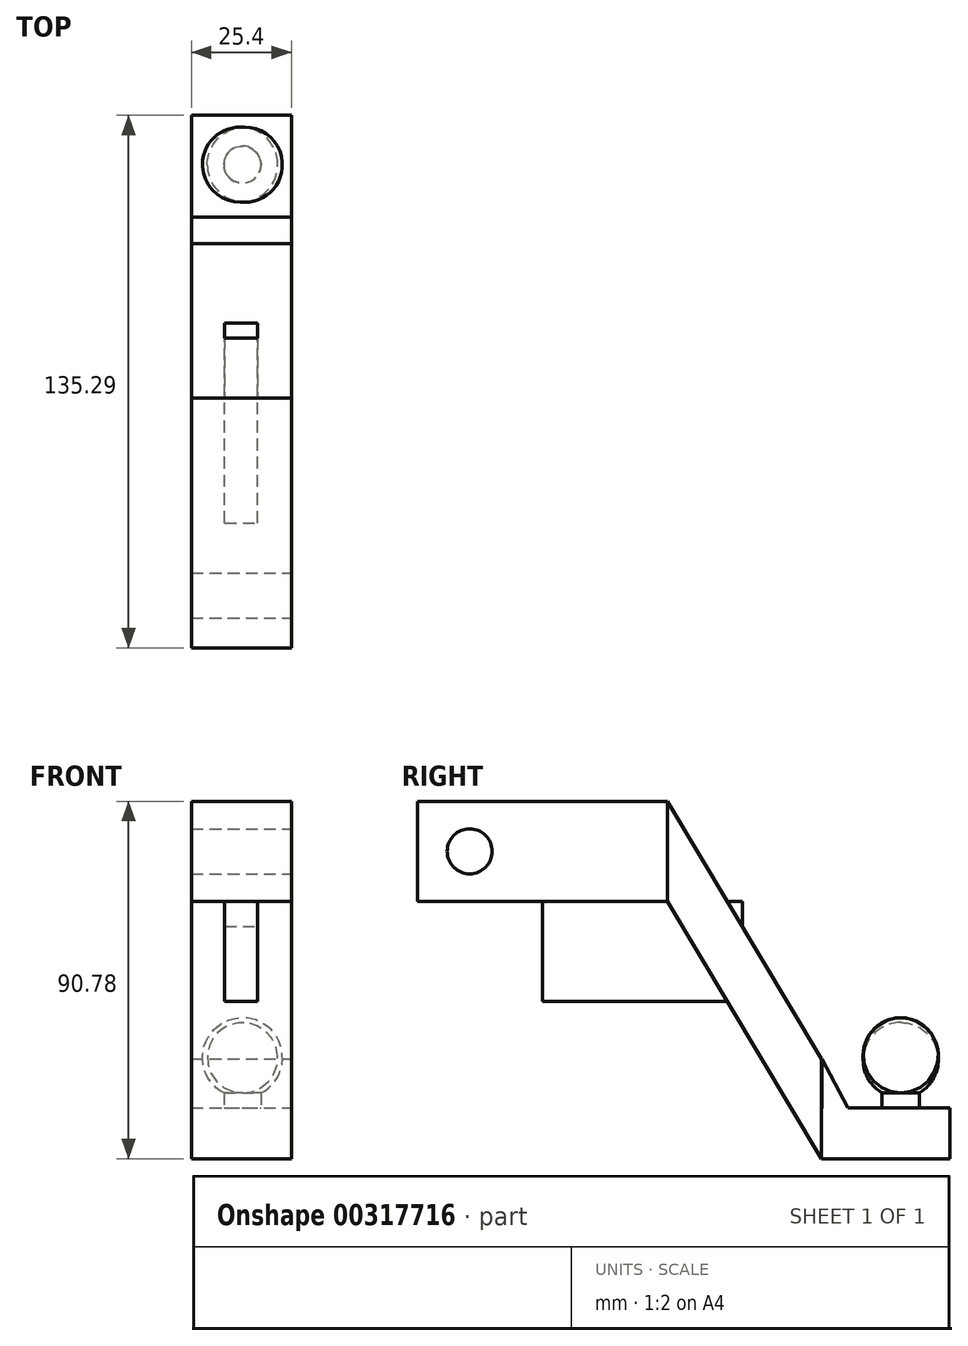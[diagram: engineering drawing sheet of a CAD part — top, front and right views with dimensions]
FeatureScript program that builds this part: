
annotation { "Feature Type Name" : "Feature", "Feature Type Description" : "" }
export const myFeature = defineFeature(function(context is Context, id is Id, definition is map)
    precondition{}
    {
        {
            var Q0;
            Q0=qCreatedBy(makeId("Front.planeOp"),FACE);
            var sketch = newSketch(context, id + "F0", { "sketchPlane" : qUnion([Q0])});
            skLineSegment(sketch, "E0", {"start": v(0, 0) * mm, "end": v(-25.4, 0) * mm});
            skLineSegment(sketch, "E1", {"start": v(-25.4, 0) * mm, "end": v(-25.4, -25.4) * mm});
            skLineSegment(sketch, "E2", {"start": v(-25.4, -25.4) * mm, "end": v(0, -25.4) * mm});
            skLineSegment(sketch, "E3", {"start": v(0, 0) * mm, "end": v(0, -25.4) * mm});
            skSolve(sketch);
        }
        {
            var Q0;
            Q0 = qSketchRegion(id + "F0", true);
            extrude(context, id + "F1", {"entities" : qUnion([Q0]), "endBound" : BoundingType.SYMMETRIC, "depth" : 63.5 * mm});
        }
        {
            var Q0;
            Q0=makeQuery(id+"F1.opExtrude","SWEPT_FACE",FACE,{"disambiguationData":[OSD([sQuery(id+"F0.wireOp",EDGE,"E3")])]});
            var sketch = newSketch(context, id + "F2", { "sketchPlane" : qUnion([Q0])});
            skCircle(sketch, "E4", {"center": v(-18.48, -12.7) * mm, "radius": 4.5 * mm});
            skSolve(sketch);
        }
        {
            var Q0;
            Q0=sQuery(id+"F2.wireOp",VERTEX,"E4.center");
            var Q1;
            Q1=makeQuery(id+"F1.opExtrude","SWEPT_BODY",BODY,{"disambiguationData":[OSD([sQuery(id+"F0.wireOp",EDGE,"E0"),sQuery(id+"F0.wireOp",EDGE,"E1"),sQuery(id+"F0.wireOp",EDGE,"E2"),sQuery(id+"F0.wireOp",EDGE,"E3")])]});
            hole(context, id + "F3", {"style" : HoleStyle.SIMPLE, "endStyle" : HoleEndStyle.BLIND, "holeDiameter" : 11.43 * mm, "holeDepth" : 25.4 * mm, "tappedDepth" : 12.7 * mm, "tapClearance" : 3, "locations" : qUnion([Q0]), "scope" : qUnion([Q1])});
        }
        {
            var Q0;
            Q0=qCreatedBy(makeId("Right.planeOp"),FACE);
            var sketch = newSketch(context, id + "F4", { "sketchPlane" : qUnion([Q0])});
            skLineSegment(sketch, "E5", {"start": v(31.78, -25.4) * mm, "end": v(70.9, -90.78) * mm});
            skLineSegment(sketch, "E6", {"start": v(70.9, -90.78) * mm, "end": v(70.9, -65.38) * mm});
            skLineSegment(sketch, "E7", {"start": v(70.9, -65.38) * mm, "end": v(31.78, 0) * mm});
            skLineSegment(sketch, "E8", {"start": v(31.78, 0) * mm, "end": v(31.78, -25.4) * mm});
            skSolve(sketch);
        }
        {
            var Q0;
            Q0 = qSketchRegion(id + "F4", true);
            extrude(context, id + "F5", {"entities" : qUnion([Q0]), "oppositeDirection" : true, "depth" : 25.4 * mm});
        }
        {
            var Q0;
            Q0=qCreatedBy(makeId("Right.planeOp"),FACE);
            var sketch = newSketch(context, id + "F6", { "sketchPlane" : qUnion([Q0])});
            skLineSegment(sketch, "E9", {"start": v(70.96, -65.45) * mm, "end": v(77.81, -78.07) * mm});
            skLineSegment(sketch, "E10", {"start": v(77.81, -78.07) * mm, "end": v(77.81, -90.77) * mm});
            skLineSegment(sketch, "E11", {"start": v(77.81, -90.77) * mm, "end": v(70.93, -90.77) * mm});
            skLineSegment(sketch, "E12", {"start": v(70.93, -90.77) * mm, "end": v(70.96, -65.45) * mm});
            skSolve(sketch);
        }
        {
            var Q0;
            Q0 = qSketchRegion(id + "F6", true);
            extrude(context, id + "F7", {"entities" : qUnion([Q0]), "oppositeDirection" : true, "depth" : 25.4 * mm});
        }
        {
            var Q0;
            Q0=qCreatedBy(makeId("Right.planeOp"),FACE);
            var sketch = newSketch(context, id + "F8", { "sketchPlane" : qUnion([Q0])});
            skLineSegment(sketch, "E13.bottom", {"start": v(74.05, -77.83) * mm, "end": v(103.54, -77.83) * mm});
            skLineSegment(sketch, "E13.top", {"start": v(74.05, -90.77) * mm, "end": v(103.54, -90.77) * mm});
            skLineSegment(sketch, "E13.left", {"start": v(74.05, -77.83) * mm, "end": v(74.05, -90.77) * mm});
            skLineSegment(sketch, "E13.right", {"start": v(103.54, -77.83) * mm, "end": v(103.54, -90.77) * mm});
            skSolve(sketch);
        }
        {
            var Q0;
            Q0 = qSketchRegion(id + "F8", true);
            extrude(context, id + "F9", {"entities" : qUnion([Q0]), "operationType" : NewBodyOperationType.ADD, "oppositeDirection" : true, "depth" : 25.4 * mm});
        }
        {
            var Q0;
            Q0=makeQuery(id+"F9.opExtrude","SWEPT_FACE",FACE,{"disambiguationData":[OSD([sQuery(id+"F8.wireOp",EDGE,"E13.bottom")])]});
            var sketch = newSketch(context, id + "F10", { "sketchPlane" : qUnion([Q0])});
            skCircle(sketch, "E14", {"center": v(-12.45, 91.03) * mm, "radius": 4.72 * mm});
            skSolve(sketch);
        }
        {
            var Q0;
            Q0=makeQuery(id+"F10.imprint","IMPRINT",FACE,{"disambiguationData":[TD([[makeQuery(id+"F10.imprint","IMPRINT",EDGE,{"derivedFrom":sQuery(id+"F10.wireOp",EDGE,"E14")}),1.0]])]});
            extrude(context, id + "F11", {"entities" : qUnion([Q0]), "operationType" : NewBodyOperationType.ADD, "depth" : 12.7 * mm});
        }
        {
            var Q0;
            Q0=makeQuery(id+"F11.opExtrude","CAP_FACE",FACE,{"disambiguationData":[OSD([sQuery(id+"F10.wireOp",EDGE,"E14")])],"isStart":false});
            var sketch = newSketch(context, id + "F12", { "sketchPlane" : qUnion([Q0])});
            skLineSegment(sketch, "E15", {"start": v(-12.45, 81.5) * mm, "end": v(-12.45, 100.56) * mm});
            skArc(sketch, "E16", {"start": v(-12.45, 81.5) * mm, "mid": v(-2.3, 91.03) * mm, "end": v(-12.45, 100.56) * mm});
            skSolve(sketch);
        }
        {
            var Q0;
            Q0 = qSketchRegion(id + "F12", true);
            var Q1;
            Q1=sQuery(id+"F12.wireOp",EDGE,"E15");
            revolve(context, id + "F13", {"operationType" : NewBodyOperationType.ADD, "entities" : qUnion([Q0]), "axis" : qUnion([Q1]), "revolveType" : RevolveType.FULL});
        }
        {
            var Q0;
            Q0=makeQuery(id+"F1.opExtrude","SWEPT_FACE",FACE,{"disambiguationData":[OSD([sQuery(id+"F0.wireOp",EDGE,"E2")])]});
            var sketch = newSketch(context, id + "F14", { "sketchPlane" : qUnion([Q0])});
            skLineSegment(sketch, "E17", {"start": v(-12.7, -31.75) * mm, "end": v(-12.7, 31.75) * mm, "construction": true});
            skSolve(sketch);
        }
        {
            var Q0;
            {var subQ0=sQuery(id+"F0.wireOp",EDGE,"E2");Q0=makeQuery(id+"F14.imprint","IMPRINT",FACE,{"disambiguationData":[TD([[makeQuery(id+"F14.imprint","IMPRINT",EDGE,{"derivedFrom":makeQuery(id+"F1.opExtrude","CAP_EDGE",EDGE,{"disambiguationData":[OSD([subQ0])],"isStart":true})}),1.0]])]});}
            var sketch = newSketch(context, id + "F15", { "sketchPlane" : qUnion([Q0])});
            skLineSegment(sketch, "E18.bottom", {"start": v(-16.94, 0) * mm, "end": v(-8.62, 0) * mm});
            skLineSegment(sketch, "E18.top", {"start": v(-16.94, -50.8) * mm, "end": v(-8.62, -50.8) * mm});
            skLineSegment(sketch, "E18.left", {"start": v(-16.94, 0) * mm, "end": v(-16.94, -50.8) * mm});
            skLineSegment(sketch, "E18.right", {"start": v(-8.62, 0) * mm, "end": v(-8.62, -50.8) * mm});
            skSolve(sketch);
        }
        {
            var Q0;
            Q0 = qSketchRegion(id + "F15", true);
            extrude(context, id + "F16", {"entities" : qUnion([Q0]), "operationType" : NewBodyOperationType.ADD, "depth" : 25.4 * mm});
        }
    });
